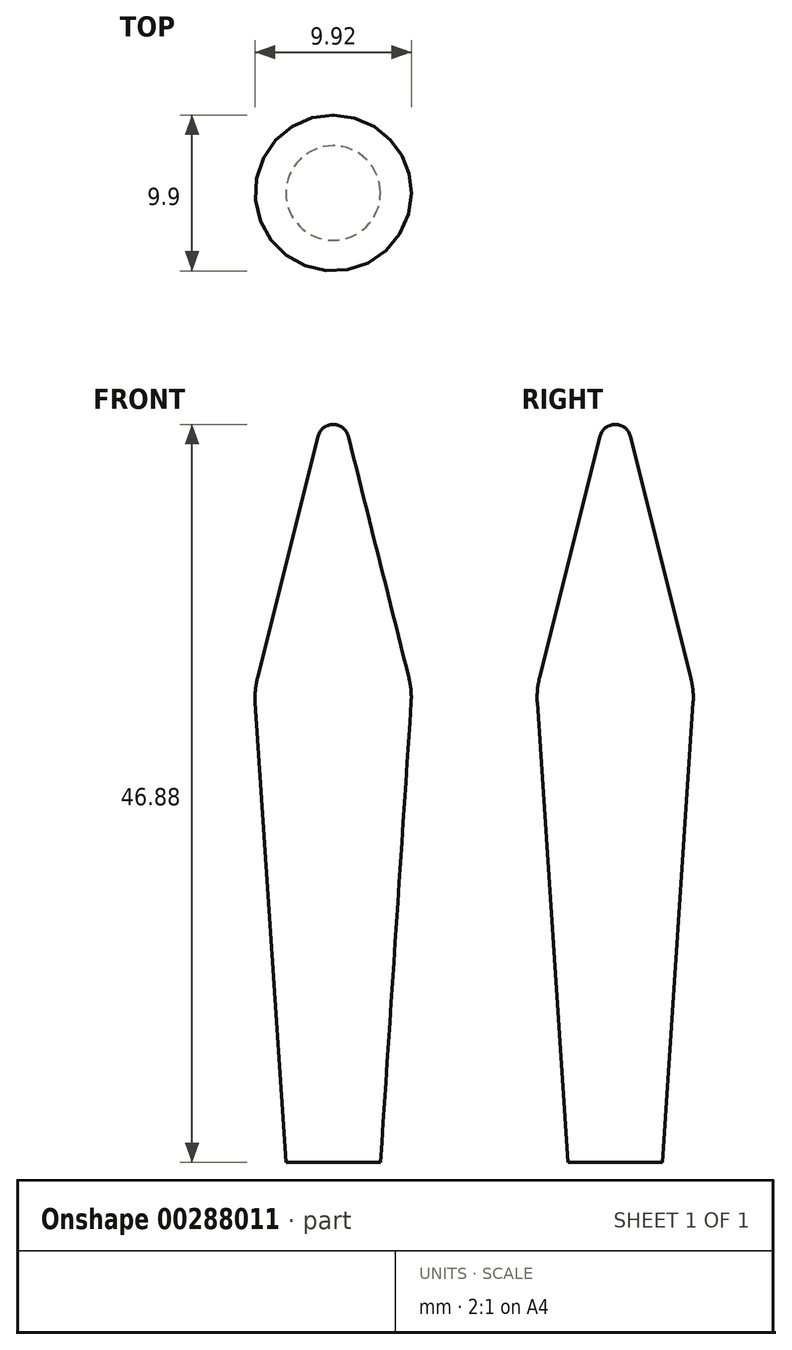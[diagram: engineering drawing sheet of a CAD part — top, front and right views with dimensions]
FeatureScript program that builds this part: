
annotation { "Feature Type Name" : "Feature", "Feature Type Description" : "" }
export const myFeature = defineFeature(function(context is Context, id is Id, definition is map)
    precondition{}
    {
        {
            var Q0;
            Q0=qCreatedBy(makeId("Front.planeOp"),FACE);
            var sketch = newSketch(context, id + "F0", { "sketchPlane" : qUnion([Q0])});
            skLineSegment(sketch, "E0", {"start": v(0.97, 46.12) * mm, "end": v(4.8, 30.76) * mm});
            skLineSegment(sketch, "E1", {"start": v(4.95, 29.22) * mm, "end": v(3, 0) * mm});
            skLineSegment(sketch, "E2", {"start": v(0, 46.88) * mm, "end": v(0, 0) * mm});
            skLineSegment(sketch, "E3", {"start": v(0, 0) * mm, "end": v(3, 0) * mm});
            skPoint(sketch, "E4.visualSharp", {"position": v(5, 30) * mm});
            skArc(sketch, "E4.filletArc", {"start": v(4.95, 29.22) * mm, "mid": v(4.94, 30) * mm, "end": v(4.8, 30.76) * mm});
            skLineSegment(sketch, "E5", {"start": v(5, 30) * mm, "end": v(5, 0) * mm, "construction": true});
            skArc(sketch, "E6", {"start": v(0.97, 46.12) * mm, "mid": v(0.62, 46.67) * mm, "end": v(0, 46.88) * mm});
            skPoint(sketch, "E7.orphan", {"position": v(0, 50) * mm});
            skSolve(sketch);
        }
        {
            var Q0;
            Q0 = qSketchRegion(id + "F0", true);
            var Q1;
            Q1=sQuery(id+"F0.wireOp",EDGE,"E2");
            revolve(context, id + "F1", {"entities" : qUnion([Q0]), "axis" : qUnion([Q1]), "revolveType" : RevolveType.FULL});
        }
    });
